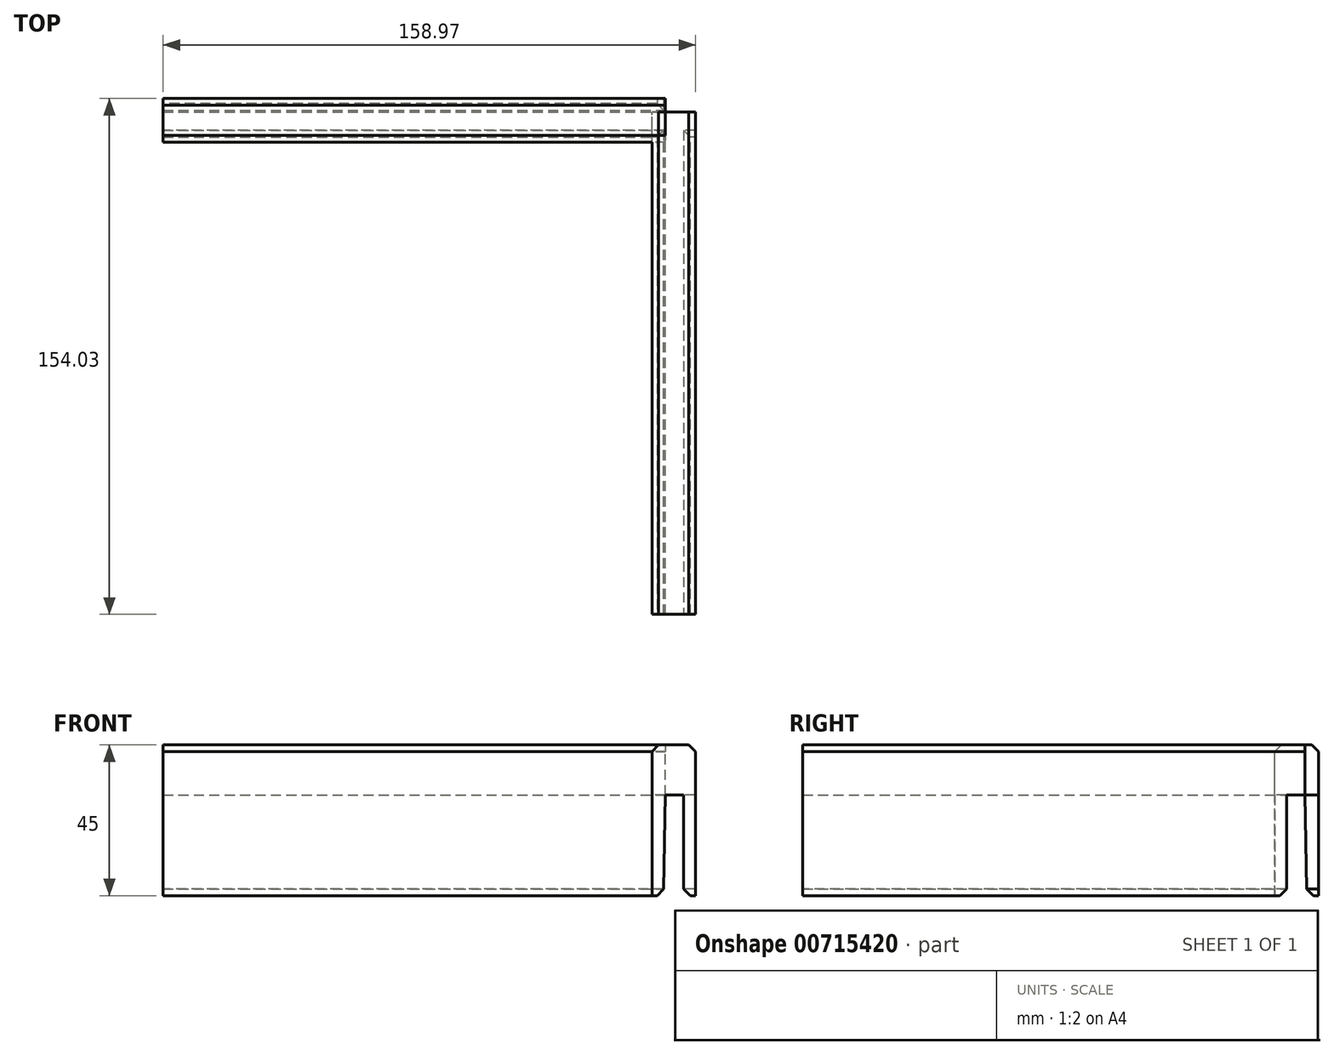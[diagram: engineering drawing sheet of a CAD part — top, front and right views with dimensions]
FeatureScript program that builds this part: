
annotation { "Feature Type Name" : "Feature", "Feature Type Description" : "" }
export const myFeature = defineFeature(function(context is Context, id is Id, definition is map)
    precondition{}
    {
        {
            var Q0;
            Q0=qCreatedBy(makeId("Front.planeOp"),FACE);
            var sketch = newSketch(context, id + "F0", { "sketchPlane" : qUnion([Q0])});
            skLineSegment(sketch, "E0", {"start": v(-0.53, 0) * mm, "end": v(-0.03, 30) * mm});
            skLineSegment(sketch, "E1", {"start": v(-0.03, 30) * mm, "end": v(5.47, 30) * mm});
            skLineSegment(sketch, "E2", {"start": v(5.47, 30) * mm, "end": v(5.47, 0) * mm});
            skLineSegment(sketch, "E3", {"start": v(5.47, 0) * mm, "end": v(8.97, 0) * mm});
            skLineSegment(sketch, "E4", {"start": v(8.97, 0) * mm, "end": v(8.97, 45) * mm});
            skLineSegment(sketch, "E5", {"start": v(8.97, 45) * mm, "end": v(-4.03, 45) * mm});
            skLineSegment(sketch, "E6", {"start": v(-4.03, 45) * mm, "end": v(-4.03, 0) * mm});
            skLineSegment(sketch, "E7", {"start": v(-4.03, 0) * mm, "end": v(-0.53, 0) * mm});
            skSolve(sketch);
        }
        {
            var Q0;
            Q0 = qSketchRegion(id + "F0", true);
            extrude(context, id + "F1", {"entities" : qUnion([Q0]), "depth" : 150 * mm, "offsetDistance" : 25 * mm});
        }
        {
            var Q0;
            Q0=makeQuery(id+"F1.opExtrude","SWEPT_EDGE",EDGE,{"disambiguationData":[OSD([sQuery(id+"F0.wireOp",EDGE,"E4"),sQuery(id+"F0.wireOp",EDGE,"E5")])]});
            var Q1;
            Q1=makeQuery(id+"F1.opExtrude","SWEPT_EDGE",EDGE,{"disambiguationData":[OSD([sQuery(id+"F0.wireOp",EDGE,"E5"),sQuery(id+"F0.wireOp",EDGE,"E6")])]});
            var Q2;
            Q2=makeQuery(id+"F1.opExtrude","SWEPT_EDGE",EDGE,{"disambiguationData":[OSD([sQuery(id+"F0.wireOp",EDGE,"E0"),sQuery(id+"F0.wireOp",EDGE,"E7")])]});
            var Q3;
            Q3=makeQuery(id+"F1.opExtrude","SWEPT_EDGE",EDGE,{"disambiguationData":[OSD([sQuery(id+"F0.wireOp",EDGE,"E2"),sQuery(id+"F0.wireOp",EDGE,"E3")])]});
            chamfer(context, id + "F2", {"entities" : qUnion([Q0, Q1, Q2, Q3]), "width" : 2 * mm, "tangentPropagation" : true});
        }
        {
            var Q0;
            Q0=makeQuery(id+"F1.opExtrude","SWEPT_BODY",BODY,{"disambiguationData":[OSD([sQuery(id+"F0.wireOp",EDGE,"E0"),sQuery(id+"F0.wireOp",EDGE,"E1"),sQuery(id+"F0.wireOp",EDGE,"E2"),sQuery(id+"F0.wireOp",EDGE,"E3"),sQuery(id+"F0.wireOp",EDGE,"E4"),sQuery(id+"F0.wireOp",EDGE,"E5"),sQuery(id+"F0.wireOp",EDGE,"E6"),sQuery(id+"F0.wireOp",EDGE,"E7")])]});
            transform(context, id + "F3", {"entities" : qUnion([Q0]), "transformType" : TransformType.TRANSLATION_3D, "dx" : 0 * mm, "dy" : 0 * mm, "dz" : 0 * mm, "makeCopy" : true});
        }
        {
            var Q0;
            Q0=qCreatedBy(makeId("Front.planeOp"),FACE);
            var sketch = newSketch(context, id + "F4", { "sketchPlane" : qUnion([Q0])});
            skLineSegment(sketch, "E8", {"start": v(0, 69.95) * mm, "end": v(0, -23.68) * mm});
            skSolve(sketch);
        }
        {
            var Q0;
            Q0=makeQuery(id+"F3.opPattern","COPY",BODY,{"derivedFrom":makeQuery(id+"F1.opExtrude","SWEPT_BODY",BODY,{"disambiguationData":[OSD([sQuery(id+"F0.wireOp",EDGE,"E0"),sQuery(id+"F0.wireOp",EDGE,"E1"),sQuery(id+"F0.wireOp",EDGE,"E2"),sQuery(id+"F0.wireOp",EDGE,"E3"),sQuery(id+"F0.wireOp",EDGE,"E4"),sQuery(id+"F0.wireOp",EDGE,"E5"),sQuery(id+"F0.wireOp",EDGE,"E6"),sQuery(id+"F0.wireOp",EDGE,"E7")])]}),"instanceName":"1"});
            var Q1;
            Q1=sQuery(id+"F4.wireOp",EDGE,"E8");
            transform(context, id + "F5", {"entities" : qUnion([Q0]), "transformType" : TransformType.ROTATION, "transformAxis" : qUnion([Q1]), "angle" : 90 * degree, "makeCopy" : true});
        }
        {
            var Q0;
            Q0=makeQuery(id+"F5.opPattern","COPY",FACE,{"derivedFrom":makeQuery(id+"F3.opPattern","COPY",FACE,{"derivedFrom":makeQuery(id+"F1.opExtrude","CAP_FACE",FACE,{"disambiguationData":[OSD([sQuery(id+"F0.wireOp",EDGE,"E0"),sQuery(id+"F0.wireOp",EDGE,"E1"),sQuery(id+"F0.wireOp",EDGE,"E2"),sQuery(id+"F0.wireOp",EDGE,"E3"),sQuery(id+"F0.wireOp",EDGE,"E4"),sQuery(id+"F0.wireOp",EDGE,"E5"),sQuery(id+"F0.wireOp",EDGE,"E6"),sQuery(id+"F0.wireOp",EDGE,"E7")])],"isStart":false}),"instanceName":"1"}),"instanceName":"1"});
            var sketch = newSketch(context, id + "F6", { "sketchPlane" : qUnion([Q0])});
            skLineSegment(sketch, "E9", {"start": v(-0.03, 30) * mm, "end": v(5.47, 30) * mm});
            skLineSegment(sketch, "E10", {"start": v(5.47, 30) * mm, "end": v(5.47, 2) * mm});
            skLineSegment(sketch, "E11", {"start": v(5.47, 0) * mm, "end": v(-0.5, 0) * mm});
            skLineSegment(sketch, "E12", {"start": v(-0.5, 0) * mm, "end": v(-0.03, 30) * mm});
            skLineSegment(sketch, "E13", {"start": v(5.47, 2) * mm, "end": v(7.47, 0) * mm});
            skLineSegment(sketch, "E14", {"start": v(7.47, 0) * mm, "end": v(5.47, 0) * mm});
            skSolve(sketch);
        }
        {
            var Q0;
            Q0=makeQuery(id+"F3.opPattern","COPY",FACE,{"derivedFrom":makeQuery(id+"F1.opExtrude","CAP_FACE",FACE,{"disambiguationData":[OSD([sQuery(id+"F0.wireOp",EDGE,"E0"),sQuery(id+"F0.wireOp",EDGE,"E1"),sQuery(id+"F0.wireOp",EDGE,"E2"),sQuery(id+"F0.wireOp",EDGE,"E3"),sQuery(id+"F0.wireOp",EDGE,"E4"),sQuery(id+"F0.wireOp",EDGE,"E5"),sQuery(id+"F0.wireOp",EDGE,"E6"),sQuery(id+"F0.wireOp",EDGE,"E7")])],"isStart":false}),"instanceName":"1"});
            var sketch = newSketch(context, id + "F7", { "sketchPlane" : qUnion([Q0])});
            skLineSegment(sketch, "E15", {"start": v(-0.03, 30) * mm, "end": v(5.47, 30) * mm});
            skLineSegment(sketch, "E16", {"start": v(5.47, 30) * mm, "end": v(5.47, 0) * mm});
            skLineSegment(sketch, "E17", {"start": v(5.47, 0) * mm, "end": v(-0.5, 0) * mm});
            skLineSegment(sketch, "E18", {"start": v(-0.5, 1.97) * mm, "end": v(-2.5, 0) * mm});
            skLineSegment(sketch, "E19", {"start": v(-2.5, 0) * mm, "end": v(-0.5, 0) * mm});
            skSolve(sketch);
        }
        {
            var Q0;
            {var subQ5=sQuery(id+"F6.wireOp",EDGE,"E9");Q0=makeQuery(id+"F6.imprint","IMPRINT",FACE,{"disambiguationData":[TD([[makeQuery(id+"F6.imprint","IMPRINT",EDGE,{"derivedFrom":subQ5}),-1.0]])]});}
            extrude(context, id + "F8", {"entities" : qUnion([Q0]), "operationType" : NewBodyOperationType.REMOVE, "endBound" : BoundingType.THROUGH_ALL, "oppositeDirection" : true, "depth" : 25 * mm, "offsetDistance" : 25 * mm});
        }
        {
            var Q0;
            {var subQ6=sQuery(id+"F7.wireOp",EDGE,"E15");Q0=makeQuery(id+"F7.imprint","IMPRINT",FACE,{"disambiguationData":[TD([[makeQuery(id+"F7.imprint","IMPRINT",EDGE,{"derivedFrom":subQ6}),-1.0]])]});}
            extrude(context, id + "F9", {"entities" : qUnion([Q0]), "operationType" : NewBodyOperationType.REMOVE, "endBound" : BoundingType.THROUGH_ALL, "oppositeDirection" : true, "depth" : 25 * mm, "offsetDistance" : 25 * mm});
        }
    });
